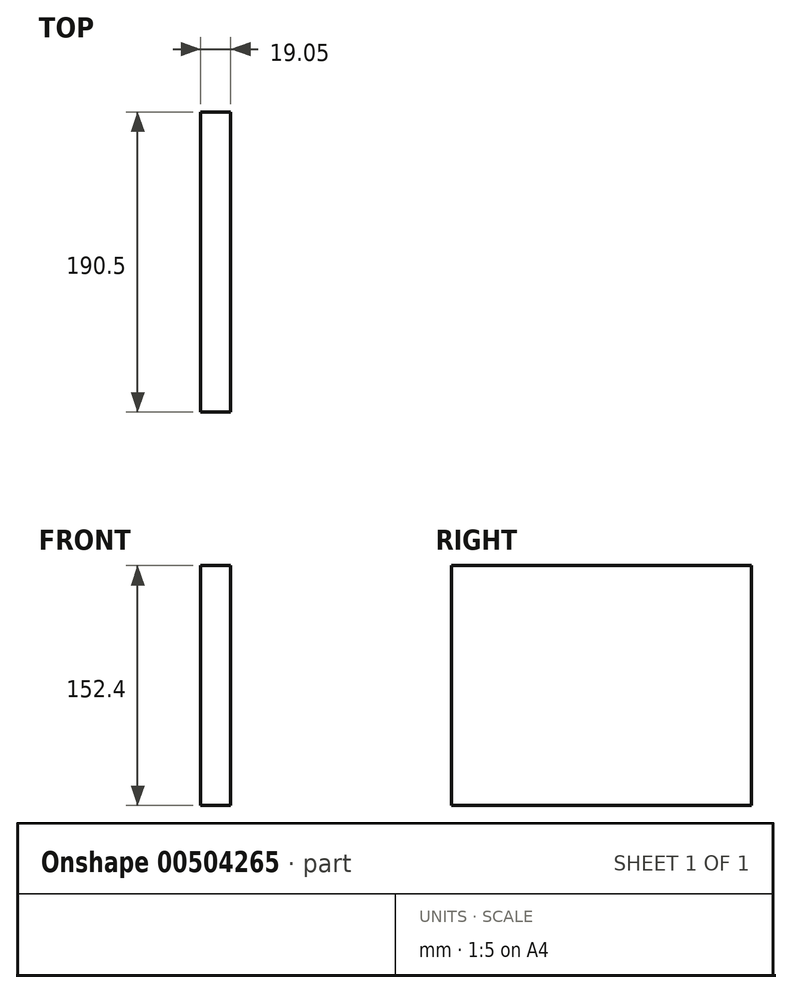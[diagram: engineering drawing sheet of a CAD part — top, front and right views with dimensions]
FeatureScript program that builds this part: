
annotation { "Feature Type Name" : "Feature", "Feature Type Description" : "" }
export const myFeature = defineFeature(function(context is Context, id is Id, definition is map)
    precondition{}
    {
        {
            var Q0;
            Q0=qCreatedBy(makeId("Right.planeOp"),FACE);
            var sketch = newSketch(context, id + "F0", { "sketchPlane" : qUnion([Q0])});
            skLineSegment(sketch, "E0.bottom", {"start": v(95.25, -76.2) * mm, "end": v(-95.25, -76.2) * mm});
            skLineSegment(sketch, "E0.top", {"start": v(95.25, 76.2) * mm, "end": v(-95.25, 76.2) * mm});
            skLineSegment(sketch, "E0.left", {"start": v(95.25, -76.2) * mm, "end": v(95.25, 76.2) * mm});
            skLineSegment(sketch, "E0.right", {"start": v(-95.25, -76.2) * mm, "end": v(-95.25, 76.2) * mm});
            skPoint(sketch, "E0.middle", {"position": v(0, 0) * mm});
            skSolve(sketch);
        }
        {
            var Q0;
            Q0=makeQuery(id+"F0.imprint","IMPRINT",FACE,{"disambiguationData":[TD([[makeQuery(id+"F0.imprint","IMPRINT",EDGE,{"derivedFrom":sQuery(id+"F0.wireOp",EDGE,"E0.bottom")}),-1.0]])]});
            extrude(context, id + "F1", {"entities" : qUnion([Q0]), "depth" : 19.05 * mm});
        }
    });
